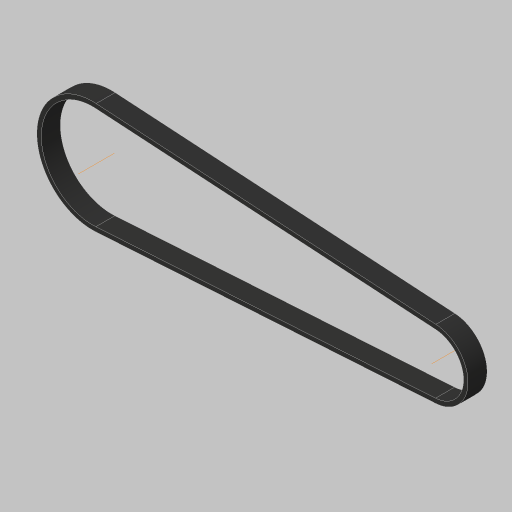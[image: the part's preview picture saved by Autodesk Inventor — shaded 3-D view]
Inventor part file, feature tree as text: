
AUTODESK INVENTOR PART (.ipt)
format: ipt  version: 2023.5 (Build 275446000, 446)  size: 163,328 bytes
history: native  units: in
note: dims shown in document units (in); Inventor stores cm internally (conversion verified against a paired STEP export)
features: sketch x3, extrude x1, other x1, projected_geometry x1
ambient origin geometry x8: Origin, YZ Plane, XZ Plane, XY Plane, X Axis, Y Axis, Z Axis, Center Point
bodies: Body1 (feature_tree)
feature tree (6):
  sketch  "Sketch2"  dims[d0=1.1279in d1=1.8798in]
  extrude  "Extrusion2"  Depth=1.8798in
  sketch  "Sketch5"  dims[d3=3.0709in d5=5.9803in d9=0.0787in d10=0.0598in d11=0.0299in d12=0.0219in d13=0.0219in d14=0.0059in d15=0.0059in d20=0.3346in d21=0.0in d22=0.0787in d23=0.0598in d24=0.0299in d25=0.0219in d26=0.0219in d27=0.0059in d28=0.0059in d29=0.0299in d30=0.0394in d31=0.0787in d32=0.0232in d34=0.0219in d35=0.0in d36=0.0in d37=0.0059in d38=0.0022in d39=0.0022in d40=0.0in d41=0.0in d42=0.0081in d43=0.0081in d44=0.0394in]
  other  "Work Axis1"
  sketch  "Sketch4"  dims[d2=1.7009in]
  projected_geometry  "Projected Loop1"
